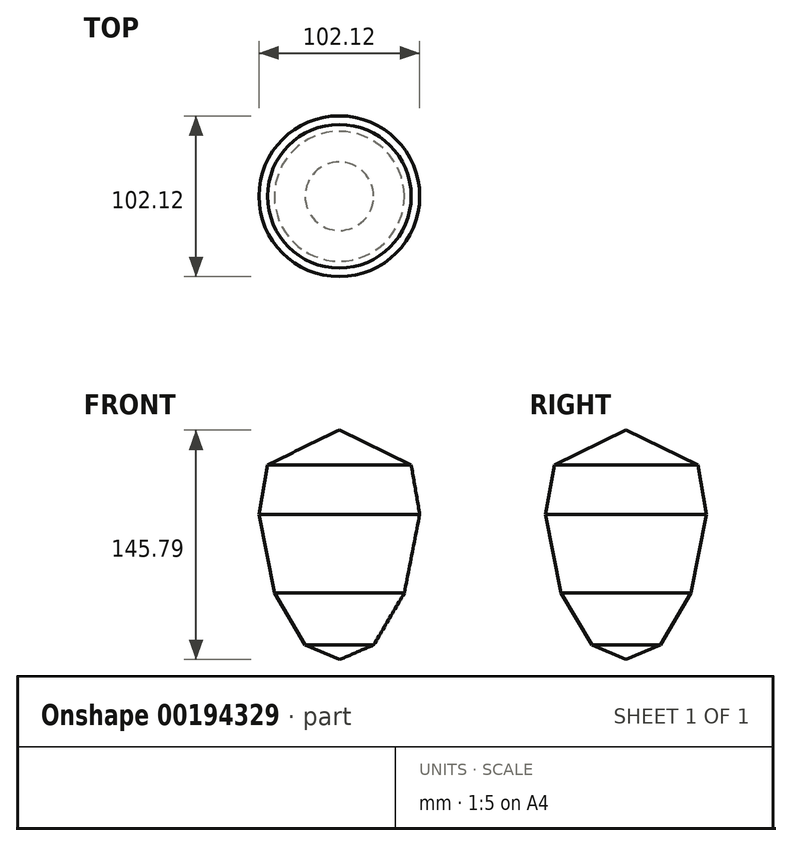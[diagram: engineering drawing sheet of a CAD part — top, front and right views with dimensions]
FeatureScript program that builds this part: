
annotation { "Feature Type Name" : "Feature", "Feature Type Description" : "" }
export const myFeature = defineFeature(function(context is Context, id is Id, definition is map)
    precondition{}
    {
        {
            var Q0;
            Q0=qCreatedBy(makeId("Front.planeOp"),FACE);
            var sketch = newSketch(context, id + "F0", { "sketchPlane" : qUnion([Q0])});
            skLineSegment(sketch, "E0", {"start": v(0, 77.73) * mm, "end": v(0, -79.25) * mm});
            skLineSegment(sketch, "E1", {"start": v(0, 71.04) * mm, "end": v(-45.6, 49.03) * mm});
            skLineSegment(sketch, "E2", {"start": v(-45.6, 49.03) * mm, "end": v(-51.06, 17.36) * mm});
            skLineSegment(sketch, "E3", {"start": v(-51.06, 17.36) * mm, "end": v(-41.23, -32.36) * mm});
            skLineSegment(sketch, "E4", {"start": v(-41.23, -32.36) * mm, "end": v(-21.75, -65.48) * mm});
            skLineSegment(sketch, "E5", {"start": v(-21.75, -65.48) * mm, "end": v(0, -74.75) * mm});
            skSolve(sketch);
        }
        {
            var Q0;
            Q0 = qSketchRegion(id + "F0", true);
            var Q1;
            Q1=sQuery(id+"F0.wireOp",EDGE,"E0");
            revolve(context, id + "F1", {"entities" : qUnion([Q0]), "axis" : qUnion([Q1]), "revolveType" : RevolveType.FULL});
        }
    });
